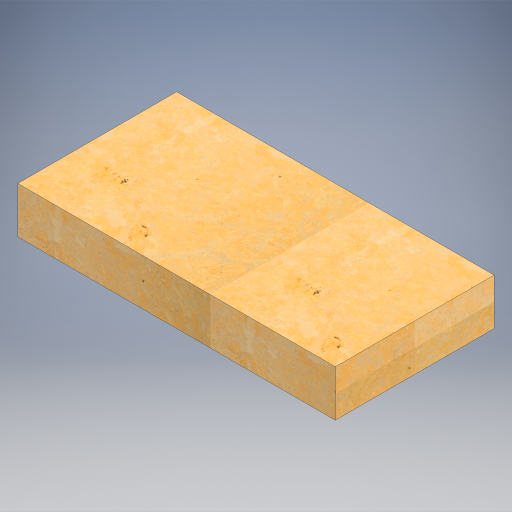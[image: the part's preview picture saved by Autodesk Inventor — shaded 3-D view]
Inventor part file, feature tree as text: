
AUTODESK INVENTOR PART (.ipt)
format: ipt  version: 2023 (Build 270158030, 158C)  size: 427,520 bytes
history: native  units: in
note: dims shown in document units (in); Inventor stores cm internally (conversion verified against a paired STEP export)
features: extrude x1, sketch x1
ambient origin geometry x8: Origin, YZ Plane, XZ Plane, XY Plane, X Axis, Y Axis, Z Axis, Center Point
bodies: Solid1 (feature_tree)
feature tree (2):
  extrude  "Extrusion1"  Depth=24.0in
  sketch  "Sketch1"  dims[d0=7.0in d1=24.0in d2=48.0in d3=0.0in]
